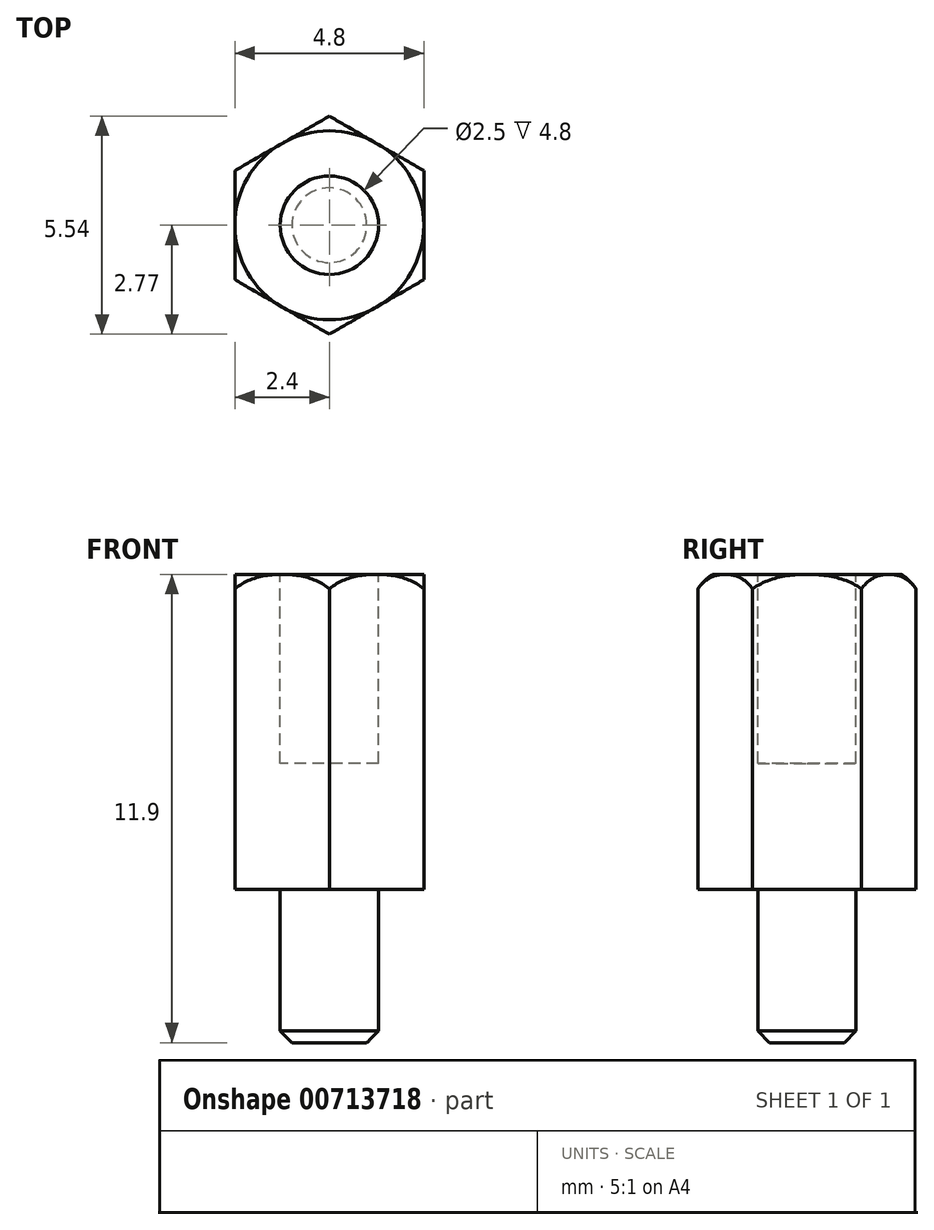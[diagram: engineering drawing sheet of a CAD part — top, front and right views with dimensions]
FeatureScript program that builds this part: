
annotation { "Feature Type Name" : "Feature", "Feature Type Description" : "" }
export const myFeature = defineFeature(function(context is Context, id is Id, definition is map)
    precondition{}
    {
        {
            var Q0;
            Q0=qCreatedBy(makeId("Top.planeOp"),FACE);
            var sketch = newSketch(context, id + "F0", { "sketchPlane" : qUnion([Q0])});
            skCircle(sketch, "E0", {"center": v(0, 0) * mm, "radius": 1.25 * mm});
            skSolve(sketch);
        }
        {
            var Q0;
            Q0=makeQuery(id+"F0.imprint","IMPRINT",FACE,{"disambiguationData":[TD([[makeQuery(id+"F0.imprint","IMPRINT",EDGE,{"derivedFrom":sQuery(id+"F0.wireOp",EDGE,"E0")}),1.0]])]});
            extrude(context, id + "F1", {"entities" : qUnion([Q0]), "depth" : 3.9 * mm});
        }
        {
            var Q0;
            Q0=makeQuery(id+"F1.opExtrude","CAP_FACE",FACE,{"disambiguationData":[OSD([sQuery(id+"F0.wireOp",EDGE,"E0")])],"isStart":false});
            var sketch = newSketch(context, id + "F2", { "sketchPlane" : qUnion([Q0])});
            skCircle(sketch, "E1.cCircle", {"center": v(0, 0) * mm, "radius": 2.4 * mm, "construction": true});
            skLineSegment(sketch, "E1.0", {"start": v(0, 2.77) * mm, "end": v(2.4, 1.39) * mm});
            skLineSegment(sketch, "E1.1", {"start": v(2.4, 1.39) * mm, "end": v(2.4, -1.39) * mm});
            skLineSegment(sketch, "E1.2", {"start": v(2.4, -1.39) * mm, "end": v(0, -2.77) * mm});
            skLineSegment(sketch, "E1.3", {"start": v(0, -2.77) * mm, "end": v(-2.4, -1.39) * mm});
            skLineSegment(sketch, "E1.4", {"start": v(-2.4, -1.39) * mm, "end": v(-2.4, 1.39) * mm});
            skLineSegment(sketch, "E1.5", {"start": v(-2.4, 1.39) * mm, "end": v(0, 2.77) * mm});
            skPoint(sketch, "E1.0.midPoint", {"position": v(1.2, 2.08) * mm});
            skSolve(sketch);
        }
        {
            var Q0;
            Q0=qSketchRegion(id+"F2",true);
            extrude(context, id + "F3", {"entities" : qUnion([Q0]), "operationType" : NewBodyOperationType.ADD, "depth" : 8 * mm});
        }
        {
            var Q0;
            Q0=makeQuery(id+"F3.opExtrude","CAP_FACE",FACE,{"disambiguationData":[OSD([sQuery(id+"F2.wireOp",EDGE,"E1.0"),sQuery(id+"F2.wireOp",EDGE,"E1.1"),sQuery(id+"F2.wireOp",EDGE,"E1.2"),sQuery(id+"F2.wireOp",EDGE,"E1.3"),sQuery(id+"F2.wireOp",EDGE,"E1.4"),sQuery(id+"F2.wireOp",EDGE,"E1.5")])],"isStart":false});
            var sketch = newSketch(context, id + "F4", { "sketchPlane" : qUnion([Q0])});
            skCircle(sketch, "E2", {"center": v(0, 0) * mm, "radius": 1.25 * mm});
            skSolve(sketch);
        }
        {
            var Q0;
            Q0=makeQuery(id+"F4.imprint","IMPRINT",FACE,{"disambiguationData":[TD([[makeQuery(id+"F4.imprint","IMPRINT",EDGE,{"derivedFrom":sQuery(id+"F4.wireOp",EDGE,"E2")}),1.0]])]});
            extrude(context, id + "F5", {"entities" : qUnion([Q0]), "operationType" : NewBodyOperationType.REMOVE, "oppositeDirection" : true, "depth" : 4.8 * mm});
        }
        {
            var Q0;
            Q0=makeQuery(id+"F3.opExtrude","CAP_FACE",FACE,{"disambiguationData":[OSD([sQuery(id+"F2.wireOp",EDGE,"E1.0"),sQuery(id+"F2.wireOp",EDGE,"E1.1"),sQuery(id+"F2.wireOp",EDGE,"E1.2"),sQuery(id+"F2.wireOp",EDGE,"E1.3"),sQuery(id+"F2.wireOp",EDGE,"E1.4"),sQuery(id+"F2.wireOp",EDGE,"E1.5")])],"isStart":false});
            var sketch = newSketch(context, id + "F6", { "sketchPlane" : qUnion([Q0])});
            skCircle(sketch, "E3", {"center": v(0, 0) * mm, "radius": 2.4 * mm});
            skSolve(sketch);
        }
        {
            var Q0;
            Q0=qCreatedBy(makeId("Right.planeOp"),FACE);
            var sketch = newSketch(context, id + "F7", { "sketchPlane" : qUnion([Q0])});
            skLineSegment(sketch, "E4.0", {"start": v(-2.4, 11.9) * mm, "end": v(2.4, 11.9) * mm, "construction": true});
            skLineSegment(sketch, "E5", {"start": v(2.4, 11.9) * mm, "end": v(2.77, 11.53) * mm, "construction": true});
            skPoint(sketch, "E6.0", {"position": v(2.77, 11.9) * mm});
            skArc(sketch, "E7", {"start": v(2.77, 11.53) * mm, "mid": v(2.6, 11.73) * mm, "end": v(2.4, 11.9) * mm});
            skLineSegment(sketch, "E8", {"start": v(2.4, 11.9) * mm, "end": v(2.77, 11.9) * mm});
            skLineSegment(sketch, "E9", {"start": v(2.77, 11.9) * mm, "end": v(2.77, 11.53) * mm});
            skSolve(sketch);
        }
        {
            var Q0;
            Q0=qSketchRegion(id+"F7",true);
            var Q1;
            Q1=sQuery(id+"F6.wireOp",EDGE,"E3");
            revolve(context, id + "F8", {"operationType" : NewBodyOperationType.REMOVE, "entities" : qUnion([Q0]), "axis" : qUnion([Q1]), "revolveType" : RevolveType.FULL, "oppositeDirection" : true});
        }
        {
            var Q0;
            Q0=makeQuery(id+"F3.opExtrude","CAP_FACE",FACE,{"disambiguationData":[OSD([sQuery(id+"F2.wireOp",EDGE,"E1.0"),sQuery(id+"F2.wireOp",EDGE,"E1.1"),sQuery(id+"F2.wireOp",EDGE,"E1.2"),sQuery(id+"F2.wireOp",EDGE,"E1.3"),sQuery(id+"F2.wireOp",EDGE,"E1.4"),sQuery(id+"F2.wireOp",EDGE,"E1.5")])],"isStart":true});
            cPlane(context, id + "F9", {"entities" : qUnion([Q0]), "cplaneType" : CPlaneType.OFFSET, "offset" : 4 * mm, "oppositeDirection" : true, "width" : 150 * mm, "height" : 150 * mm});
        }
        {
            var Q0;
            Q0=makeQuery(id+"F1.opExtrude","CAP_EDGE",EDGE,{"disambiguationData":[OSD([sQuery(id+"F0.wireOp",EDGE,"E0")])],"isStart":true});
            chamfer(context, id + "F10", {"entities" : qUnion([Q0]), "width" : .3 * mm, "tangentPropagation" : true});
        }
    });
